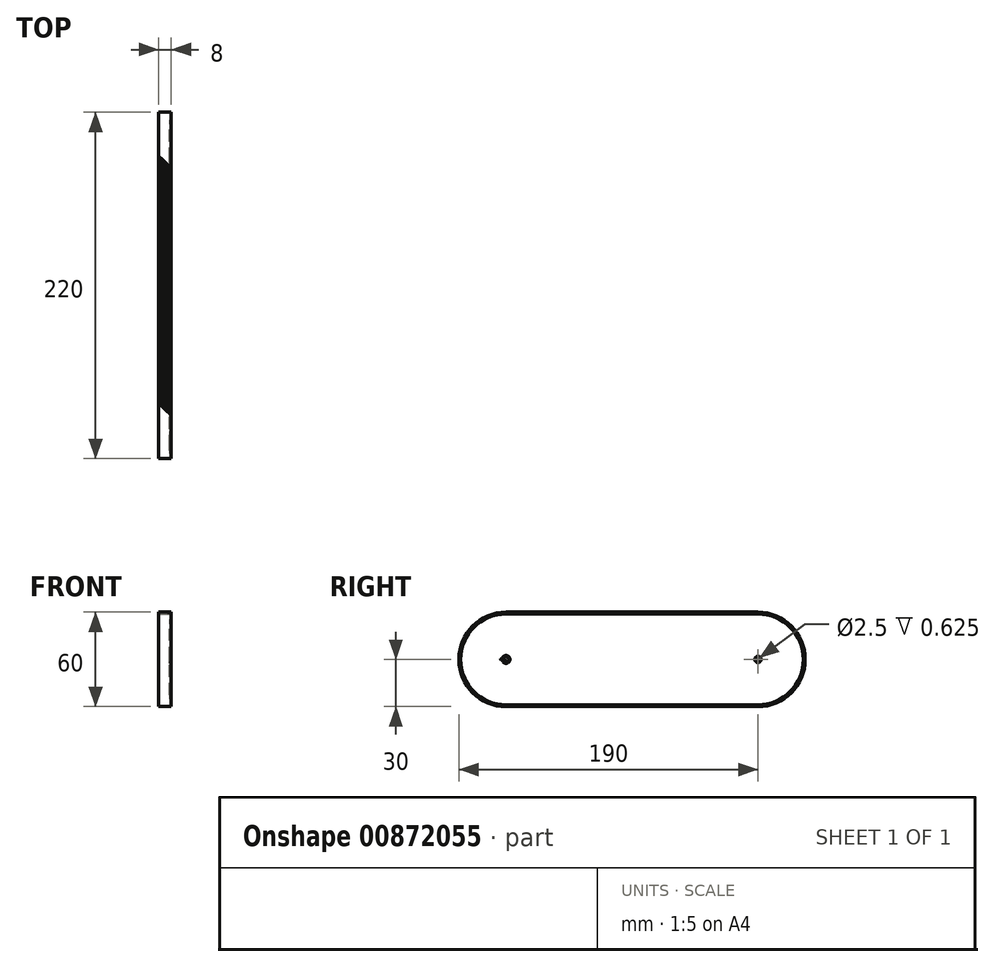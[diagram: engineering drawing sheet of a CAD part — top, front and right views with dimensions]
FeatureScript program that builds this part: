
annotation { "Feature Type Name" : "Feature", "Feature Type Description" : "" }
export const myFeature = defineFeature(function(context is Context, id is Id, definition is map)
    precondition{}
    {
        {
            var Q0;
            Q0=qCreatedBy(makeId("Right.planeOp"),FACE);
            var sketch = newSketch(context, id + "F0", { "sketchPlane" : qUnion([Q0])});
            skLineSegment(sketch, "E0.bottom", {"start": v(80, -30) * mm, "end": v(-80, -30) * mm});
            skLineSegment(sketch, "E0.top", {"start": v(80, 30) * mm, "end": v(-80, 30) * mm});
            skLineSegment(sketch, "E0.left", {"start": v(110, 0) * mm, "end": v(110, 0) * mm});
            skLineSegment(sketch, "E0.right", {"start": v(-110, 0) * mm, "end": v(-110, 0) * mm});
            skPoint(sketch, "E0.middle", {"position": v(0, 0) * mm});
            skPoint(sketch, "E1.visualSharp", {"position": v(-110, 30) * mm});
            skArc(sketch, "E1.filletArc", {"start": v(-80, 30) * mm, "mid": v(-101.21, 21.21) * mm, "end": v(-110, 0) * mm});
            skPoint(sketch, "E2.visualSharp", {"position": v(-110, -30) * mm});
            skArc(sketch, "E2.filletArc", {"start": v(-110, 0) * mm, "mid": v(-101.21, -21.21) * mm, "end": v(-80, -30) * mm});
            skPoint(sketch, "E3.visualSharp", {"position": v(110, -30) * mm});
            skArc(sketch, "E3.filletArc", {"start": v(80, -30) * mm, "mid": v(101.21, -21.21) * mm, "end": v(110, 0) * mm});
            skPoint(sketch, "E4.visualSharp", {"position": v(110, 30) * mm});
            skArc(sketch, "E4.filletArc", {"start": v(110, 0) * mm, "mid": v(101.21, 21.21) * mm, "end": v(80, 30) * mm});
            skSolve(sketch);
        }
        {
            var Q0;
            Q0=makeQuery(id+"F0.imprint","IMPRINT",FACE,{"disambiguationData":[TD([[makeQuery(id+"F0.imprint","IMPRINT",EDGE,{"derivedFrom":sQuery(id+"F0.wireOp",EDGE,"E0.bottom")}),-1.0]])]});
            extrude(context, id + "F1", {"entities" : qUnion([Q0]), "depth" : 8 * mm, "offsetDistance" : 25 * mm});
        }
        {
            var Q0;
            Q0=makeQuery(id+"F1.opExtrude","CAP_FACE",FACE,{"disambiguationData":[OSD([sQuery(id+"F0.wireOp",EDGE,"E0.bottom"),sQuery(id+"F0.wireOp",EDGE,"E0.top"),sQuery(id+"F0.wireOp",EDGE,"E1.filletArc"),sQuery(id+"F0.wireOp",EDGE,"E2.filletArc"),sQuery(id+"F0.wireOp",EDGE,"E3.filletArc"),sQuery(id+"F0.wireOp",EDGE,"E4.filletArc")])],"isStart":false});
            var sketch = newSketch(context, id + "F2", { "sketchPlane" : qUnion([Q0])});
            skLineSegment(sketch, "E5.left", {"start": v(110, 0) * mm, "end": v(110, 0) * mm});
            skLineSegment(sketch, "E5.right", {"start": v(-110, 0) * mm, "end": v(-110, 0) * mm});
            skPoint(sketch, "E5.middle", {"position": v(0, 0) * mm});
            skPoint(sketch, "E6.visualSharp", {"position": v(-110, 30) * mm});
            skPoint(sketch, "E7.visualSharp", {"position": v(-110, -30) * mm});
            skPoint(sketch, "E8.visualSharp", {"position": v(110, -30) * mm});
            skPoint(sketch, "E9.visualSharp", {"position": v(110, 30) * mm});
            skArc(sketch, "E10.0", {"start": v(108.8, 0) * mm, "mid": v(100.36, 20.36) * mm, "end": v(80, 28.8) * mm});
            skArc(sketch, "E10.1", {"start": v(-80, 28.8) * mm, "mid": v(-100.36, 20.36) * mm, "end": v(-108.8, 0) * mm});
            skArc(sketch, "E10.2", {"start": v(-108.8, 0) * mm, "mid": v(-100.36, -20.36) * mm, "end": v(-80, -28.8) * mm});
            skLineSegment(sketch, "E10.3", {"start": v(80, 28.8) * mm, "end": v(-80, 28.8) * mm});
            skLineSegment(sketch, "E10.4", {"start": v(80, -28.8) * mm, "end": v(-80, -28.8) * mm});
            skArc(sketch, "E10.5", {"start": v(80, -28.8) * mm, "mid": v(100.36, -20.36) * mm, "end": v(108.8, 0) * mm});
            skSolve(sketch);
        }
        {
            var Q0;
            Q0=makeQuery(id+"F2.imprint","IMPRINT",FACE,{"disambiguationData":[TD([[makeQuery(id+"F2.imprint","IMPRINT",EDGE,{"derivedFrom":sQuery(id+"F2.wireOp",EDGE,"E10.0")}),1.0]])]});
            extrude(context, id + "F3", {"entities" : qUnion([Q0]), "operationType" : NewBodyOperationType.REMOVE, "oppositeDirection" : true, "depth" : 1 * mm, "offsetDistance" : 25 * mm});
        }
        {
            var Q0;
            Q0=makeQuery(id+"F3.boolean.opBoolean","COPY",EDGE,{"derivedFrom":makeQuery(id+"F3.opExtrude","CAP_EDGE",EDGE,{"disambiguationData":[OSD([sQuery(id+"F2.wireOp",EDGE,"E10.3")])],"isStart":false})});
            fillet(context, id + "F4", {"entities" : qUnion([Q0]), "radius" : 20 * mm, "tangentPropagation" : true, "allowEdgeOverflow" : false});
        }
        {
            var Q0;
            Q0=makeQuery(id+"F3.boolean.opBoolean","COPY",FACE,{"derivedFrom":makeQuery(id+"F3.opExtrude","CAP_FACE",FACE,{"disambiguationData":[OSD([sQuery(id+"F2.wireOp",EDGE,"E10.0"),sQuery(id+"F2.wireOp",EDGE,"E10.1"),sQuery(id+"F2.wireOp",EDGE,"E10.2"),sQuery(id+"F2.wireOp",EDGE,"E10.3"),sQuery(id+"F2.wireOp",EDGE,"E10.4"),sQuery(id+"F2.wireOp",EDGE,"E10.5")])],"isStart":false})});
            var sketch = newSketch(context, id + "F5", { "sketchPlane" : qUnion([Q0])});
            skPoint(sketch, "E11", {"position": v(-80, 0) * mm});
            skArc(sketch, "E12", {"start": v(-82.27, -1.04) * mm, "mid": v(-77.5, 0) * mm, "end": v(-82.27, 1.04) * mm});
            skArc(sketch, "E13.0", {"start": v(-81.6, -0.73) * mm, "mid": v(-78.25, 0) * mm, "end": v(-81.6, 0.73) * mm});
            skLineSegment(sketch, "E14", {"start": v(-81.02, 0) * mm, "end": v(-83.02, 0) * mm});
            skArc(sketch, "E15.0.startCap", {"start": v(-81.02, 0.38) * mm, "mid": v(-80.64, 0) * mm, "end": v(-81.02, -0.37) * mm});
            skArc(sketch, "E15.0.endCap", {"start": v(-83.02, -0.37) * mm, "mid": v(-83.4, 0) * mm, "end": v(-83.02, 0.38) * mm});
            skLineSegment(sketch, "E15.0.left", {"start": v(-81.02, -0.37) * mm, "end": v(-83.02, -0.37) * mm});
            skLineSegment(sketch, "E15.0.right", {"start": v(-81.02, 0.38) * mm, "end": v(-83.02, 0.38) * mm});
            skArc(sketch, "E16", {"start": v(-81.6, -0.73) * mm, "mid": v(-82.08, -0.56) * mm, "end": v(-82.27, -1.04) * mm});
            skArc(sketch, "E17", {"start": v(-82.27, 1.04) * mm, "mid": v(-82.09, 0.55) * mm, "end": v(-81.6, 0.73) * mm});
            skLineSegment(sketch, "E18", {"start": v(-80, 0) * mm, "end": v(-81.93, 0.9) * mm});
            skSolve(sketch);
        }
        {
            var Q0;
            Q0 = qSketchRegion(id + "F5", true);
            extrude(context, id + "F6", {"entities" : qUnion([Q0]), "operationType" : NewBodyOperationType.ADD, "depth" : 1 * mm, "offsetDistance" : 25 * mm});
        }
        {
            var Q0;
            Q0=makeQuery(id+"F3.boolean.opBoolean","COPY",FACE,{"derivedFrom":makeQuery(id+"F3.opExtrude","CAP_FACE",FACE,{"disambiguationData":[OSD([sQuery(id+"F2.wireOp",EDGE,"E10.0"),sQuery(id+"F2.wireOp",EDGE,"E10.1"),sQuery(id+"F2.wireOp",EDGE,"E10.2"),sQuery(id+"F2.wireOp",EDGE,"E10.3"),sQuery(id+"F2.wireOp",EDGE,"E10.4"),sQuery(id+"F2.wireOp",EDGE,"E10.5")])],"isStart":false})});
            var sketch = newSketch(context, id + "F7", { "sketchPlane" : qUnion([Q0])});
            skPoint(sketch, "E19", {"position": v(80, 0) * mm});
            skCircle(sketch, "E20", {"center": v(80, 0) * mm, "radius": 2 * mm});
            skCircle(sketch, "E21.0", {"center": v(80, 0) * mm, "radius": 1.25 * mm});
            skSolve(sketch);
        }
        {
            var Q0;
            Q0 = qSketchRegion(id + "F7", true);
            extrude(context, id + "F8", {"entities" : qUnion([Q0]), "operationType" : NewBodyOperationType.ADD, "depth" : 1 * mm, "offsetDistance" : 25 * mm});
        }
        {
            var Q0;
            Q0=makeQuery(id+"F6.opExtrude","CAP_EDGE",EDGE,{"disambiguationData":[OSD([sQuery(id+"F5.wireOp",EDGE,"E12")])],"isStart":false});
            var Q1;
            Q1=makeQuery(id+"F6.opExtrude","CAP_EDGE",EDGE,{"disambiguationData":[OSD([sQuery(id+"F5.wireOp",EDGE,"E13.0")])],"isStart":false});
            var Q2;
            Q2=makeQuery(id+"F6.opExtrude","CAP_EDGE",EDGE,{"disambiguationData":[OSD([sQuery(id+"F5.wireOp",EDGE,"E16")])],"isStart":false});
            var Q3;
            Q3=makeQuery(id+"F6.opExtrude","CAP_EDGE",EDGE,{"disambiguationData":[OSD([sQuery(id+"F5.wireOp",EDGE,"E17")])],"isStart":false});
            var Q4;
            Q4=makeQuery(id+"F6.opExtrude","CAP_EDGE",EDGE,{"disambiguationData":[OSD([sQuery(id+"F5.wireOp",EDGE,"E15.0.startCap")])],"isStart":false});
            var Q5;
            Q5=makeQuery(id+"F6.opExtrude","CAP_EDGE",EDGE,{"disambiguationData":[OSD([sQuery(id+"F5.wireOp",EDGE,"E15.0.endCap")])],"isStart":false});
            var Q6;
            Q6=makeQuery(id+"F6.opExtrude","CAP_EDGE",EDGE,{"disambiguationData":[OSD([sQuery(id+"F5.wireOp",EDGE,"E15.0.right")])],"isStart":false});
            var Q7;
            Q7=makeQuery(id+"F6.opExtrude","CAP_EDGE",EDGE,{"disambiguationData":[OSD([sQuery(id+"F5.wireOp",EDGE,"E15.0.left")])],"isStart":false});
            fillet(context, id + "F9", {"entities" : qUnion([Q0, Q1, Q2, Q3, Q4, Q5, Q6, Q7]), "radius" : 0.38 * mm, "tangentPropagation" : true, "allowEdgeOverflow" : false});
        }
        {
            var Q0;
            Q0=makeQuery(id+"F8.opExtrude","CAP_EDGE",EDGE,{"disambiguationData":[OSD([sQuery(id+"F7.wireOp",EDGE,"E21.0")])],"isStart":false});
            var Q1;
            Q1=makeQuery(id+"F8.opExtrude","CAP_EDGE",EDGE,{"disambiguationData":[OSD([sQuery(id+"F7.wireOp",EDGE,"E20")])],"isStart":false});
            fillet(context, id + "F10", {"entities" : qUnion([Q0, Q1]), "radius" : 0.38 * mm, "tangentPropagation" : true, "allowEdgeOverflow" : false});
        }
        {
            var Q0;
            Q0=makeQuery(id+"F1.opExtrude","SWEPT_FACE",FACE,{"disambiguationData":[OSD([sQuery(id+"F0.wireOp",EDGE,"E0.top")])]});
            var sketch = newSketch(context, id + "F11", { "sketchPlane" : qUnion([Q0])});
            skPoint(sketch, "E22", {"position": v(4, 0) * mm});
            skArc(sketch, "E23.0.startCap", {"start": v(0.9, 2.56) * mm, "mid": v(0.9, 3.1) * mm, "end": v(1.44, 3.1) * mm});
            skArc(sketch, "E23.0.endCap", {"start": v(7.1, -2.56) * mm, "mid": v(7.1, -3.1) * mm, "end": v(6.56, -3.1) * mm});
            skLineSegment(sketch, "E23.0.left", {"start": v(1.44, 3.1) * mm, "end": v(7.1, -2.56) * mm});
            skLineSegment(sketch, "E23.0.right", {"start": v(0.9, 2.56) * mm, "end": v(6.56, -3.1) * mm});
            skLineSegment(sketch, "E24", {"start": v(4, 0) * mm, "end": v(4, 2.2) * mm});
            skArc(sketch, "E25.0.1.0", {"start": v(0.9, 5.56) * mm, "mid": v(0.9, 6.1) * mm, "end": v(1.44, 6.1) * mm});
            skLineSegment(sketch, "E25.0.1.1", {"start": v(1.44, 6.1) * mm, "end": v(7.1, 0.44) * mm});
            skArc(sketch, "E25.0.1.2", {"start": v(7.1, 0.44) * mm, "mid": v(7.1, -0.1) * mm, "end": v(6.56, -0.1) * mm});
            skLineSegment(sketch, "E25.0.1.3", {"start": v(0.9, 5.56) * mm, "end": v(6.56, -0.1) * mm});
            skArc(sketch, "E25.0.2.0", {"start": v(0.9, 8.56) * mm, "mid": v(0.9, 9.1) * mm, "end": v(1.44, 9.1) * mm});
            skLineSegment(sketch, "E25.0.2.1", {"start": v(1.44, 9.1) * mm, "end": v(7.1, 3.44) * mm});
            skArc(sketch, "E25.0.2.2", {"start": v(7.1, 3.44) * mm, "mid": v(7.1, 2.9) * mm, "end": v(6.56, 2.9) * mm});
            skLineSegment(sketch, "E25.0.2.3", {"start": v(0.9, 8.56) * mm, "end": v(6.56, 2.9) * mm});
            skArc(sketch, "E25.0.3.0", {"start": v(0.9, 11.56) * mm, "mid": v(0.9, 12.1) * mm, "end": v(1.44, 12.1) * mm});
            skLineSegment(sketch, "E25.0.3.1", {"start": v(1.44, 12.1) * mm, "end": v(7.1, 6.44) * mm});
            skArc(sketch, "E25.0.3.2", {"start": v(7.1, 6.44) * mm, "mid": v(7.1, 5.9) * mm, "end": v(6.56, 5.9) * mm});
            skLineSegment(sketch, "E25.0.3.3", {"start": v(0.9, 11.56) * mm, "end": v(6.56, 5.9) * mm});
            skArc(sketch, "E25.0.4.0", {"start": v(0.9, 14.56) * mm, "mid": v(0.9, 15.1) * mm, "end": v(1.44, 15.1) * mm});
            skLineSegment(sketch, "E25.0.4.1", {"start": v(1.44, 15.1) * mm, "end": v(7.1, 9.44) * mm});
            skArc(sketch, "E25.0.4.2", {"start": v(7.1, 9.44) * mm, "mid": v(7.1, 8.9) * mm, "end": v(6.56, 8.9) * mm});
            skLineSegment(sketch, "E25.0.4.3", {"start": v(0.9, 14.56) * mm, "end": v(6.56, 8.9) * mm});
            skArc(sketch, "E25.0.5.0", {"start": v(0.9, 17.56) * mm, "mid": v(0.9, 18.1) * mm, "end": v(1.44, 18.1) * mm});
            skLineSegment(sketch, "E25.0.5.1", {"start": v(1.44, 18.1) * mm, "end": v(7.1, 12.44) * mm});
            skArc(sketch, "E25.0.5.2", {"start": v(7.1, 12.44) * mm, "mid": v(7.1, 11.9) * mm, "end": v(6.56, 11.9) * mm});
            skLineSegment(sketch, "E25.0.5.3", {"start": v(0.9, 17.56) * mm, "end": v(6.56, 11.9) * mm});
            skArc(sketch, "E25.0.6.0", {"start": v(0.9, 20.56) * mm, "mid": v(0.9, 21.1) * mm, "end": v(1.44, 21.1) * mm});
            skLineSegment(sketch, "E25.0.6.1", {"start": v(1.44, 21.1) * mm, "end": v(7.1, 15.44) * mm});
            skArc(sketch, "E25.0.6.2", {"start": v(7.1, 15.44) * mm, "mid": v(7.1, 14.9) * mm, "end": v(6.56, 14.9) * mm});
            skLineSegment(sketch, "E25.0.6.3", {"start": v(0.9, 20.56) * mm, "end": v(6.56, 14.9) * mm});
            skArc(sketch, "E25.0.7.0", {"start": v(0.9, 23.56) * mm, "mid": v(0.9, 24.1) * mm, "end": v(1.44, 24.1) * mm});
            skLineSegment(sketch, "E25.0.7.1", {"start": v(1.44, 24.1) * mm, "end": v(7.1, 18.44) * mm});
            skArc(sketch, "E25.0.7.2", {"start": v(7.1, 18.44) * mm, "mid": v(7.1, 17.9) * mm, "end": v(6.56, 17.9) * mm});
            skLineSegment(sketch, "E25.0.7.3", {"start": v(0.9, 23.56) * mm, "end": v(6.56, 17.9) * mm});
            skArc(sketch, "E25.0.8.0", {"start": v(0.9, 26.56) * mm, "mid": v(0.9, 27.1) * mm, "end": v(1.44, 27.1) * mm});
            skLineSegment(sketch, "E25.0.8.1", {"start": v(1.44, 27.1) * mm, "end": v(7.1, 21.44) * mm});
            skArc(sketch, "E25.0.8.2", {"start": v(7.1, 21.44) * mm, "mid": v(7.1, 20.9) * mm, "end": v(6.56, 20.9) * mm});
            skLineSegment(sketch, "E25.0.8.3", {"start": v(0.9, 26.56) * mm, "end": v(6.56, 20.9) * mm});
            skArc(sketch, "E25.0.9.0", {"start": v(0.9, 29.56) * mm, "mid": v(0.9, 30.1) * mm, "end": v(1.44, 30.1) * mm});
            skLineSegment(sketch, "E25.0.9.1", {"start": v(1.44, 30.1) * mm, "end": v(7.1, 24.44) * mm});
            skArc(sketch, "E25.0.9.2", {"start": v(7.1, 24.44) * mm, "mid": v(7.1, 23.9) * mm, "end": v(6.56, 23.9) * mm});
            skLineSegment(sketch, "E25.0.9.3", {"start": v(0.9, 29.56) * mm, "end": v(6.56, 23.9) * mm});
            skArc(sketch, "E25.0.10.0", {"start": v(0.9, 32.56) * mm, "mid": v(0.9, 33.1) * mm, "end": v(1.44, 33.1) * mm});
            skLineSegment(sketch, "E25.0.10.1", {"start": v(1.44, 33.1) * mm, "end": v(7.1, 27.44) * mm});
            skArc(sketch, "E25.0.10.2", {"start": v(7.1, 27.44) * mm, "mid": v(7.1, 26.9) * mm, "end": v(6.56, 26.9) * mm});
            skLineSegment(sketch, "E25.0.10.3", {"start": v(0.9, 32.56) * mm, "end": v(6.56, 26.9) * mm});
            skArc(sketch, "E25.0.11.0", {"start": v(0.9, 35.56) * mm, "mid": v(0.9, 36.1) * mm, "end": v(1.44, 36.1) * mm});
            skLineSegment(sketch, "E25.0.11.1", {"start": v(1.44, 36.1) * mm, "end": v(7.1, 30.44) * mm});
            skArc(sketch, "E25.0.11.2", {"start": v(7.1, 30.44) * mm, "mid": v(7.1, 29.9) * mm, "end": v(6.56, 29.9) * mm});
            skLineSegment(sketch, "E25.0.11.3", {"start": v(0.9, 35.56) * mm, "end": v(6.56, 29.9) * mm});
            skArc(sketch, "E25.0.12.0", {"start": v(0.9, 38.56) * mm, "mid": v(0.9, 39.1) * mm, "end": v(1.44, 39.1) * mm});
            skLineSegment(sketch, "E25.0.12.1", {"start": v(1.44, 39.1) * mm, "end": v(7.1, 33.44) * mm});
            skArc(sketch, "E25.0.12.2", {"start": v(7.1, 33.44) * mm, "mid": v(7.1, 32.9) * mm, "end": v(6.56, 32.9) * mm});
            skLineSegment(sketch, "E25.0.12.3", {"start": v(0.9, 38.56) * mm, "end": v(6.56, 32.9) * mm});
            skArc(sketch, "E25.0.13.0", {"start": v(0.9, 41.56) * mm, "mid": v(0.9, 42.1) * mm, "end": v(1.44, 42.1) * mm});
            skLineSegment(sketch, "E25.0.13.1", {"start": v(1.44, 42.1) * mm, "end": v(7.1, 36.44) * mm});
            skArc(sketch, "E25.0.13.2", {"start": v(7.1, 36.44) * mm, "mid": v(7.1, 35.9) * mm, "end": v(6.56, 35.9) * mm});
            skLineSegment(sketch, "E25.0.13.3", {"start": v(0.9, 41.56) * mm, "end": v(6.56, 35.9) * mm});
            skArc(sketch, "E25.0.14.0", {"start": v(0.9, 44.56) * mm, "mid": v(0.9, 45.1) * mm, "end": v(1.44, 45.1) * mm});
            skLineSegment(sketch, "E25.0.14.1", {"start": v(1.44, 45.1) * mm, "end": v(7.1, 39.44) * mm});
            skArc(sketch, "E25.0.14.2", {"start": v(7.1, 39.44) * mm, "mid": v(7.1, 38.9) * mm, "end": v(6.56, 38.9) * mm});
            skLineSegment(sketch, "E25.0.14.3", {"start": v(0.9, 44.56) * mm, "end": v(6.56, 38.9) * mm});
            skArc(sketch, "E25.0.15.0", {"start": v(0.9, 47.56) * mm, "mid": v(0.9, 48.1) * mm, "end": v(1.44, 48.1) * mm});
            skLineSegment(sketch, "E25.0.15.1", {"start": v(1.44, 48.1) * mm, "end": v(7.1, 42.44) * mm});
            skArc(sketch, "E25.0.15.2", {"start": v(7.1, 42.44) * mm, "mid": v(7.1, 41.9) * mm, "end": v(6.56, 41.9) * mm});
            skLineSegment(sketch, "E25.0.15.3", {"start": v(0.9, 47.56) * mm, "end": v(6.56, 41.9) * mm});
            skArc(sketch, "E25.0.16.0", {"start": v(0.9, 50.56) * mm, "mid": v(0.9, 51.1) * mm, "end": v(1.44, 51.1) * mm});
            skLineSegment(sketch, "E25.0.16.1", {"start": v(1.44, 51.1) * mm, "end": v(7.1, 45.44) * mm});
            skArc(sketch, "E25.0.16.2", {"start": v(7.1, 45.44) * mm, "mid": v(7.1, 44.9) * mm, "end": v(6.56, 44.9) * mm});
            skLineSegment(sketch, "E25.0.16.3", {"start": v(0.9, 50.56) * mm, "end": v(6.56, 44.9) * mm});
            skArc(sketch, "E25.0.17.0", {"start": v(0.9, 53.56) * mm, "mid": v(0.9, 54.1) * mm, "end": v(1.44, 54.1) * mm});
            skLineSegment(sketch, "E25.0.17.1", {"start": v(1.44, 54.1) * mm, "end": v(7.1, 48.44) * mm});
            skArc(sketch, "E25.0.17.2", {"start": v(7.1, 48.44) * mm, "mid": v(7.1, 47.9) * mm, "end": v(6.56, 47.9) * mm});
            skLineSegment(sketch, "E25.0.17.3", {"start": v(0.9, 53.56) * mm, "end": v(6.56, 47.9) * mm});
            skArc(sketch, "E25.0.18.0", {"start": v(0.9, 56.56) * mm, "mid": v(0.9, 57.1) * mm, "end": v(1.44, 57.1) * mm});
            skLineSegment(sketch, "E25.0.18.1", {"start": v(1.44, 57.1) * mm, "end": v(7.1, 51.44) * mm});
            skArc(sketch, "E25.0.18.2", {"start": v(7.1, 51.44) * mm, "mid": v(7.1, 50.9) * mm, "end": v(6.56, 50.9) * mm});
            skLineSegment(sketch, "E25.0.18.3", {"start": v(0.9, 56.56) * mm, "end": v(6.56, 50.9) * mm});
            skArc(sketch, "E25.0.19.0", {"start": v(0.9, 59.56) * mm, "mid": v(0.9, 60.1) * mm, "end": v(1.44, 60.1) * mm});
            skLineSegment(sketch, "E25.0.19.1", {"start": v(1.44, 60.1) * mm, "end": v(7.1, 54.44) * mm});
            skArc(sketch, "E25.0.19.2", {"start": v(7.1, 54.44) * mm, "mid": v(7.1, 53.9) * mm, "end": v(6.56, 53.9) * mm});
            skLineSegment(sketch, "E25.0.19.3", {"start": v(0.9, 59.56) * mm, "end": v(6.56, 53.9) * mm});
            skArc(sketch, "E25.0.20.0", {"start": v(0.9, 62.56) * mm, "mid": v(0.9, 63.1) * mm, "end": v(1.44, 63.1) * mm});
            skLineSegment(sketch, "E25.0.20.1", {"start": v(1.44, 63.1) * mm, "end": v(7.1, 57.44) * mm});
            skArc(sketch, "E25.0.20.2", {"start": v(7.1, 57.44) * mm, "mid": v(7.1, 56.9) * mm, "end": v(6.56, 56.9) * mm});
            skLineSegment(sketch, "E25.0.20.3", {"start": v(0.9, 62.56) * mm, "end": v(6.56, 56.9) * mm});
            skArc(sketch, "E25.0.21.0", {"start": v(0.9, 65.56) * mm, "mid": v(0.9, 66.1) * mm, "end": v(1.44, 66.1) * mm});
            skLineSegment(sketch, "E25.0.21.1", {"start": v(1.44, 66.1) * mm, "end": v(7.1, 60.44) * mm});
            skArc(sketch, "E25.0.21.2", {"start": v(7.1, 60.44) * mm, "mid": v(7.1, 59.9) * mm, "end": v(6.56, 59.9) * mm});
            skLineSegment(sketch, "E25.0.21.3", {"start": v(0.9, 65.56) * mm, "end": v(6.56, 59.9) * mm});
            skArc(sketch, "E25.0.22.0", {"start": v(0.9, 68.56) * mm, "mid": v(0.9, 69.1) * mm, "end": v(1.44, 69.1) * mm});
            skLineSegment(sketch, "E25.0.22.1", {"start": v(1.44, 69.1) * mm, "end": v(7.1, 63.44) * mm});
            skArc(sketch, "E25.0.22.2", {"start": v(7.1, 63.44) * mm, "mid": v(7.1, 62.9) * mm, "end": v(6.56, 62.9) * mm});
            skLineSegment(sketch, "E25.0.22.3", {"start": v(0.9, 68.56) * mm, "end": v(6.56, 62.9) * mm});
            skArc(sketch, "E25.0.23.0", {"start": v(0.9, 71.56) * mm, "mid": v(0.9, 72.1) * mm, "end": v(1.44, 72.1) * mm});
            skLineSegment(sketch, "E25.0.23.1", {"start": v(1.44, 72.1) * mm, "end": v(7.1, 66.44) * mm});
            skArc(sketch, "E25.0.23.2", {"start": v(7.1, 66.44) * mm, "mid": v(7.1, 65.9) * mm, "end": v(6.56, 65.9) * mm});
            skLineSegment(sketch, "E25.0.23.3", {"start": v(0.9, 71.56) * mm, "end": v(6.56, 65.9) * mm});
            skArc(sketch, "E25.0.24.0", {"start": v(0.9, 74.56) * mm, "mid": v(0.9, 75.1) * mm, "end": v(1.44, 75.1) * mm});
            skLineSegment(sketch, "E25.0.24.1", {"start": v(1.44, 75.1) * mm, "end": v(7.1, 69.44) * mm});
            skArc(sketch, "E25.0.24.2", {"start": v(7.1, 69.44) * mm, "mid": v(7.1, 68.9) * mm, "end": v(6.56, 68.9) * mm});
            skLineSegment(sketch, "E25.0.24.3", {"start": v(0.9, 74.56) * mm, "end": v(6.56, 68.9) * mm});
            skArc(sketch, "E25.0.25.0", {"start": v(0.9, 77.56) * mm, "mid": v(0.9, 78.1) * mm, "end": v(1.44, 78.1) * mm});
            skLineSegment(sketch, "E25.0.25.1", {"start": v(1.44, 78.1) * mm, "end": v(7.1, 72.44) * mm});
            skArc(sketch, "E25.0.25.2", {"start": v(7.1, 72.44) * mm, "mid": v(7.1, 71.9) * mm, "end": v(6.56, 71.9) * mm});
            skLineSegment(sketch, "E25.0.25.3", {"start": v(0.9, 77.56) * mm, "end": v(6.56, 71.9) * mm});
            skArc(sketch, "E25.0.26.0", {"start": v(0.9, 80.56) * mm, "mid": v(0.9, 81.1) * mm, "end": v(1.44, 81.1) * mm});
            skLineSegment(sketch, "E25.0.26.1", {"start": v(1.44, 81.1) * mm, "end": v(7.1, 75.44) * mm});
            skArc(sketch, "E25.0.26.2", {"start": v(7.1, 75.44) * mm, "mid": v(7.1, 74.9) * mm, "end": v(6.56, 74.9) * mm});
            skLineSegment(sketch, "E25.0.26.3", {"start": v(0.9, 80.56) * mm, "end": v(6.56, 74.9) * mm});
            skLineSegment(sketch, "E25.direction1", {"start": v(0.9, 2.56) * mm, "end": v(25.9, 2.56) * mm, "construction": true});
            skLineSegment(sketch, "E25.direction2", {"start": v(0.9, 2.56) * mm, "end": v(0.9, 5.56) * mm, "construction": true});
            skSolve(sketch);
        }
        {
            var Q0;
            {var subQ3=sQuery(id+"F11.wireOp",EDGE,"E23.0.startCap");Q0=makeQuery(id+"F11.imprint","IMPRINT",FACE,{"disambiguationData":[TD([[makeQuery(id+"F11.imprint","IMPRINT",EDGE,{"derivedFrom":subQ3}),1.0]])]});}
            var sketch = newSketch(context, id + "F12", { "sketchPlane" : qUnion([Q0])});
            skArc(sketch, "E26.0.startCap", {"start": v(0.9, 2.56) * mm, "mid": v(0.9, 3.1) * mm, "end": v(1.44, 3.1) * mm});
            skArc(sketch, "E26.0.endCap", {"start": v(7.1, -2.56) * mm, "mid": v(7.1, -3.1) * mm, "end": v(6.56, -3.1) * mm});
            skLineSegment(sketch, "E26.0.left", {"start": v(1.44, 3.1) * mm, "end": v(7.1, -2.56) * mm});
            skLineSegment(sketch, "E26.0.right", {"start": v(0.9, 2.56) * mm, "end": v(6.56, -3.1) * mm});
            skArc(sketch, "E27.0.1.0", {"start": v(7.1, -5.56) * mm, "mid": v(7.1, -6.1) * mm, "end": v(6.56, -6.1) * mm});
            skLineSegment(sketch, "E27.0.1.1", {"start": v(1.44, 0.1) * mm, "end": v(7.1, -5.56) * mm});
            skLineSegment(sketch, "E27.0.1.2", {"start": v(0.9, -0.44) * mm, "end": v(6.56, -6.1) * mm});
            skArc(sketch, "E27.0.1.3", {"start": v(0.9, -0.44) * mm, "mid": v(0.9, 0.1) * mm, "end": v(1.44, 0.1) * mm});
            skArc(sketch, "E27.0.2.0", {"start": v(7.1, -8.56) * mm, "mid": v(7.1, -9.1) * mm, "end": v(6.56, -9.1) * mm});
            skLineSegment(sketch, "E27.0.2.1", {"start": v(1.44, -2.9) * mm, "end": v(7.1, -8.56) * mm});
            skLineSegment(sketch, "E27.0.2.2", {"start": v(0.9, -3.44) * mm, "end": v(6.56, -9.1) * mm});
            skArc(sketch, "E27.0.2.3", {"start": v(0.9, -3.44) * mm, "mid": v(0.9, -2.9) * mm, "end": v(1.44, -2.9) * mm});
            skArc(sketch, "E27.0.3.0", {"start": v(7.1, -11.56) * mm, "mid": v(7.1, -12.1) * mm, "end": v(6.56, -12.1) * mm});
            skLineSegment(sketch, "E27.0.3.1", {"start": v(1.44, -5.9) * mm, "end": v(7.1, -11.56) * mm});
            skLineSegment(sketch, "E27.0.3.2", {"start": v(0.9, -6.44) * mm, "end": v(6.56, -12.1) * mm});
            skArc(sketch, "E27.0.3.3", {"start": v(0.9, -6.44) * mm, "mid": v(0.9, -5.9) * mm, "end": v(1.44, -5.9) * mm});
            skArc(sketch, "E27.0.4.0", {"start": v(7.1, -14.56) * mm, "mid": v(7.1, -15.1) * mm, "end": v(6.56, -15.1) * mm});
            skLineSegment(sketch, "E27.0.4.1", {"start": v(1.44, -8.9) * mm, "end": v(7.1, -14.56) * mm});
            skLineSegment(sketch, "E27.0.4.2", {"start": v(0.9, -9.44) * mm, "end": v(6.56, -15.1) * mm});
            skArc(sketch, "E27.0.4.3", {"start": v(0.9, -9.44) * mm, "mid": v(0.9, -8.9) * mm, "end": v(1.44, -8.9) * mm});
            skArc(sketch, "E27.0.5.0", {"start": v(7.1, -17.56) * mm, "mid": v(7.1, -18.1) * mm, "end": v(6.56, -18.1) * mm});
            skLineSegment(sketch, "E27.0.5.1", {"start": v(1.44, -11.9) * mm, "end": v(7.1, -17.56) * mm});
            skLineSegment(sketch, "E27.0.5.2", {"start": v(0.9, -12.44) * mm, "end": v(6.56, -18.1) * mm});
            skArc(sketch, "E27.0.5.3", {"start": v(0.9, -12.44) * mm, "mid": v(0.9, -11.9) * mm, "end": v(1.44, -11.9) * mm});
            skArc(sketch, "E27.0.6.0", {"start": v(7.1, -20.56) * mm, "mid": v(7.1, -21.1) * mm, "end": v(6.56, -21.1) * mm});
            skLineSegment(sketch, "E27.0.6.1", {"start": v(1.44, -14.9) * mm, "end": v(7.1, -20.56) * mm});
            skLineSegment(sketch, "E27.0.6.2", {"start": v(0.9, -15.44) * mm, "end": v(6.56, -21.1) * mm});
            skArc(sketch, "E27.0.6.3", {"start": v(0.9, -15.44) * mm, "mid": v(0.9, -14.9) * mm, "end": v(1.44, -14.9) * mm});
            skArc(sketch, "E27.0.7.0", {"start": v(7.1, -23.56) * mm, "mid": v(7.1, -24.1) * mm, "end": v(6.56, -24.1) * mm});
            skLineSegment(sketch, "E27.0.7.1", {"start": v(1.44, -17.9) * mm, "end": v(7.1, -23.56) * mm});
            skLineSegment(sketch, "E27.0.7.2", {"start": v(0.9, -18.44) * mm, "end": v(6.56, -24.1) * mm});
            skArc(sketch, "E27.0.7.3", {"start": v(0.9, -18.44) * mm, "mid": v(0.9, -17.9) * mm, "end": v(1.44, -17.9) * mm});
            skArc(sketch, "E27.0.8.0", {"start": v(7.1, -26.56) * mm, "mid": v(7.1, -27.1) * mm, "end": v(6.56, -27.1) * mm});
            skLineSegment(sketch, "E27.0.8.1", {"start": v(1.44, -20.9) * mm, "end": v(7.1, -26.56) * mm});
            skLineSegment(sketch, "E27.0.8.2", {"start": v(0.9, -21.44) * mm, "end": v(6.56, -27.1) * mm});
            skArc(sketch, "E27.0.8.3", {"start": v(0.9, -21.44) * mm, "mid": v(0.9, -20.9) * mm, "end": v(1.44, -20.9) * mm});
            skArc(sketch, "E27.0.9.0", {"start": v(7.1, -29.56) * mm, "mid": v(7.1, -30.1) * mm, "end": v(6.56, -30.1) * mm});
            skLineSegment(sketch, "E27.0.9.1", {"start": v(1.44, -23.9) * mm, "end": v(7.1, -29.56) * mm});
            skLineSegment(sketch, "E27.0.9.2", {"start": v(0.9, -24.44) * mm, "end": v(6.56, -30.1) * mm});
            skArc(sketch, "E27.0.9.3", {"start": v(0.9, -24.44) * mm, "mid": v(0.9, -23.9) * mm, "end": v(1.44, -23.9) * mm});
            skArc(sketch, "E27.0.10.0", {"start": v(7.1, -32.56) * mm, "mid": v(7.1, -33.1) * mm, "end": v(6.56, -33.1) * mm});
            skLineSegment(sketch, "E27.0.10.1", {"start": v(1.44, -26.9) * mm, "end": v(7.1, -32.56) * mm});
            skLineSegment(sketch, "E27.0.10.2", {"start": v(0.9, -27.44) * mm, "end": v(6.56, -33.1) * mm});
            skArc(sketch, "E27.0.10.3", {"start": v(0.9, -27.44) * mm, "mid": v(0.9, -26.9) * mm, "end": v(1.44, -26.9) * mm});
            skArc(sketch, "E27.0.11.0", {"start": v(7.1, -35.56) * mm, "mid": v(7.1, -36.1) * mm, "end": v(6.56, -36.1) * mm});
            skLineSegment(sketch, "E27.0.11.1", {"start": v(1.44, -29.9) * mm, "end": v(7.1, -35.56) * mm});
            skLineSegment(sketch, "E27.0.11.2", {"start": v(0.9, -30.44) * mm, "end": v(6.56, -36.1) * mm});
            skArc(sketch, "E27.0.11.3", {"start": v(0.9, -30.44) * mm, "mid": v(0.9, -29.9) * mm, "end": v(1.44, -29.9) * mm});
            skArc(sketch, "E27.0.12.0", {"start": v(7.1, -38.56) * mm, "mid": v(7.1, -39.1) * mm, "end": v(6.56, -39.1) * mm});
            skLineSegment(sketch, "E27.0.12.1", {"start": v(1.44, -32.9) * mm, "end": v(7.1, -38.56) * mm});
            skLineSegment(sketch, "E27.0.12.2", {"start": v(0.9, -33.44) * mm, "end": v(6.56, -39.1) * mm});
            skArc(sketch, "E27.0.12.3", {"start": v(0.9, -33.44) * mm, "mid": v(0.9, -32.9) * mm, "end": v(1.44, -32.9) * mm});
            skArc(sketch, "E27.0.13.0", {"start": v(7.1, -41.56) * mm, "mid": v(7.1, -42.1) * mm, "end": v(6.56, -42.1) * mm});
            skLineSegment(sketch, "E27.0.13.1", {"start": v(1.44, -35.9) * mm, "end": v(7.1, -41.56) * mm});
            skLineSegment(sketch, "E27.0.13.2", {"start": v(0.9, -36.44) * mm, "end": v(6.56, -42.1) * mm});
            skArc(sketch, "E27.0.13.3", {"start": v(0.9, -36.44) * mm, "mid": v(0.9, -35.9) * mm, "end": v(1.44, -35.9) * mm});
            skArc(sketch, "E27.0.14.0", {"start": v(7.1, -44.56) * mm, "mid": v(7.1, -45.1) * mm, "end": v(6.56, -45.1) * mm});
            skLineSegment(sketch, "E27.0.14.1", {"start": v(1.44, -38.9) * mm, "end": v(7.1, -44.56) * mm});
            skLineSegment(sketch, "E27.0.14.2", {"start": v(0.9, -39.44) * mm, "end": v(6.56, -45.1) * mm});
            skArc(sketch, "E27.0.14.3", {"start": v(0.9, -39.44) * mm, "mid": v(0.9, -38.9) * mm, "end": v(1.44, -38.9) * mm});
            skArc(sketch, "E27.0.15.0", {"start": v(7.1, -47.56) * mm, "mid": v(7.1, -48.1) * mm, "end": v(6.56, -48.1) * mm});
            skLineSegment(sketch, "E27.0.15.1", {"start": v(1.44, -41.9) * mm, "end": v(7.1, -47.56) * mm});
            skLineSegment(sketch, "E27.0.15.2", {"start": v(0.9, -42.44) * mm, "end": v(6.56, -48.1) * mm});
            skArc(sketch, "E27.0.15.3", {"start": v(0.9, -42.44) * mm, "mid": v(0.9, -41.9) * mm, "end": v(1.44, -41.9) * mm});
            skArc(sketch, "E27.0.16.0", {"start": v(7.1, -50.56) * mm, "mid": v(7.1, -51.1) * mm, "end": v(6.56, -51.1) * mm});
            skLineSegment(sketch, "E27.0.16.1", {"start": v(1.44, -44.9) * mm, "end": v(7.1, -50.56) * mm});
            skLineSegment(sketch, "E27.0.16.2", {"start": v(0.9, -45.44) * mm, "end": v(6.56, -51.1) * mm});
            skArc(sketch, "E27.0.16.3", {"start": v(0.9, -45.44) * mm, "mid": v(0.9, -44.9) * mm, "end": v(1.44, -44.9) * mm});
            skArc(sketch, "E27.0.17.0", {"start": v(7.1, -53.56) * mm, "mid": v(7.1, -54.1) * mm, "end": v(6.56, -54.1) * mm});
            skLineSegment(sketch, "E27.0.17.1", {"start": v(1.44, -47.9) * mm, "end": v(7.1, -53.56) * mm});
            skLineSegment(sketch, "E27.0.17.2", {"start": v(0.9, -48.44) * mm, "end": v(6.56, -54.1) * mm});
            skArc(sketch, "E27.0.17.3", {"start": v(0.9, -48.44) * mm, "mid": v(0.9, -47.9) * mm, "end": v(1.44, -47.9) * mm});
            skArc(sketch, "E27.0.18.0", {"start": v(7.1, -56.56) * mm, "mid": v(7.1, -57.1) * mm, "end": v(6.56, -57.1) * mm});
            skLineSegment(sketch, "E27.0.18.1", {"start": v(1.44, -50.9) * mm, "end": v(7.1, -56.56) * mm});
            skLineSegment(sketch, "E27.0.18.2", {"start": v(0.9, -51.44) * mm, "end": v(6.56, -57.1) * mm});
            skArc(sketch, "E27.0.18.3", {"start": v(0.9, -51.44) * mm, "mid": v(0.9, -50.9) * mm, "end": v(1.44, -50.9) * mm});
            skArc(sketch, "E27.0.19.0", {"start": v(7.1, -59.56) * mm, "mid": v(7.1, -60.1) * mm, "end": v(6.56, -60.1) * mm});
            skLineSegment(sketch, "E27.0.19.1", {"start": v(1.44, -53.9) * mm, "end": v(7.1, -59.56) * mm});
            skLineSegment(sketch, "E27.0.19.2", {"start": v(0.9, -54.44) * mm, "end": v(6.56, -60.1) * mm});
            skArc(sketch, "E27.0.19.3", {"start": v(0.9, -54.44) * mm, "mid": v(0.9, -53.9) * mm, "end": v(1.44, -53.9) * mm});
            skArc(sketch, "E27.0.20.0", {"start": v(7.1, -62.56) * mm, "mid": v(7.1, -63.1) * mm, "end": v(6.56, -63.1) * mm});
            skLineSegment(sketch, "E27.0.20.1", {"start": v(1.44, -56.9) * mm, "end": v(7.1, -62.56) * mm});
            skLineSegment(sketch, "E27.0.20.2", {"start": v(0.9, -57.44) * mm, "end": v(6.56, -63.1) * mm});
            skArc(sketch, "E27.0.20.3", {"start": v(0.9, -57.44) * mm, "mid": v(0.9, -56.9) * mm, "end": v(1.44, -56.9) * mm});
            skArc(sketch, "E27.0.21.0", {"start": v(7.1, -65.56) * mm, "mid": v(7.1, -66.1) * mm, "end": v(6.56, -66.1) * mm});
            skLineSegment(sketch, "E27.0.21.1", {"start": v(1.44, -59.9) * mm, "end": v(7.1, -65.56) * mm});
            skLineSegment(sketch, "E27.0.21.2", {"start": v(0.9, -60.44) * mm, "end": v(6.56, -66.1) * mm});
            skArc(sketch, "E27.0.21.3", {"start": v(0.9, -60.44) * mm, "mid": v(0.9, -59.9) * mm, "end": v(1.44, -59.9) * mm});
            skArc(sketch, "E27.0.22.0", {"start": v(7.1, -68.56) * mm, "mid": v(7.1, -69.1) * mm, "end": v(6.56, -69.1) * mm});
            skLineSegment(sketch, "E27.0.22.1", {"start": v(1.44, -62.9) * mm, "end": v(7.1, -68.56) * mm});
            skLineSegment(sketch, "E27.0.22.2", {"start": v(0.9, -63.44) * mm, "end": v(6.56, -69.1) * mm});
            skArc(sketch, "E27.0.22.3", {"start": v(0.9, -63.44) * mm, "mid": v(0.9, -62.9) * mm, "end": v(1.44, -62.9) * mm});
            skArc(sketch, "E27.0.23.0", {"start": v(7.1, -71.56) * mm, "mid": v(7.1, -72.1) * mm, "end": v(6.56, -72.1) * mm});
            skLineSegment(sketch, "E27.0.23.1", {"start": v(1.44, -65.9) * mm, "end": v(7.1, -71.56) * mm});
            skLineSegment(sketch, "E27.0.23.2", {"start": v(0.9, -66.44) * mm, "end": v(6.56, -72.1) * mm});
            skArc(sketch, "E27.0.23.3", {"start": v(0.9, -66.44) * mm, "mid": v(0.9, -65.9) * mm, "end": v(1.44, -65.9) * mm});
            skArc(sketch, "E27.0.24.0", {"start": v(7.1, -74.56) * mm, "mid": v(7.1, -75.1) * mm, "end": v(6.56, -75.1) * mm});
            skLineSegment(sketch, "E27.0.24.1", {"start": v(1.44, -68.9) * mm, "end": v(7.1, -74.56) * mm});
            skLineSegment(sketch, "E27.0.24.2", {"start": v(0.9, -69.44) * mm, "end": v(6.56, -75.1) * mm});
            skArc(sketch, "E27.0.24.3", {"start": v(0.9, -69.44) * mm, "mid": v(0.9, -68.9) * mm, "end": v(1.44, -68.9) * mm});
            skArc(sketch, "E27.0.25.0", {"start": v(7.1, -77.56) * mm, "mid": v(7.1, -78.1) * mm, "end": v(6.56, -78.1) * mm});
            skLineSegment(sketch, "E27.0.25.1", {"start": v(1.44, -71.9) * mm, "end": v(7.1, -77.56) * mm});
            skLineSegment(sketch, "E27.0.25.2", {"start": v(0.9, -72.44) * mm, "end": v(6.56, -78.1) * mm});
            skArc(sketch, "E27.0.25.3", {"start": v(0.9, -72.44) * mm, "mid": v(0.9, -71.9) * mm, "end": v(1.44, -71.9) * mm});
            skLineSegment(sketch, "E27.direction1", {"start": v(6.56, -3.1) * mm, "end": v(31.56, -3.1) * mm, "construction": true});
            skLineSegment(sketch, "E27.direction2", {"start": v(6.56, -3.1) * mm, "end": v(6.56, -6.1) * mm, "construction": true});
            skArc(sketch, "E28.0.0.26", {"start": v(7.1, -80.56) * mm, "mid": v(7.1, -81.1) * mm, "end": v(6.56, -81.1) * mm});
            skLineSegment(sketch, "E28.4.0.26", {"start": v(1.44, -74.9) * mm, "end": v(7.1, -80.56) * mm});
            skLineSegment(sketch, "E28.7.0.26", {"start": v(0.9, -75.44) * mm, "end": v(6.56, -81.1) * mm});
            skArc(sketch, "E28.10.0.26", {"start": v(0.9, -75.44) * mm, "mid": v(0.9, -74.9) * mm, "end": v(1.44, -74.9) * mm});
            skSolve(sketch);
        }
        {
            var Q0;
            Q0 = qSketchRegion(id + "F11", true);
            var Q1;
            Q1 = qSketchRegion(id + "F12", true);
            extrude(context, id + "F13", {"entities" : qUnion([Q0, Q1]), "operationType" : NewBodyOperationType.REMOVE, "oppositeDirection" : true, "depth" : 1 * mm, "offsetDistance" : 25 * mm});
        }
    });
